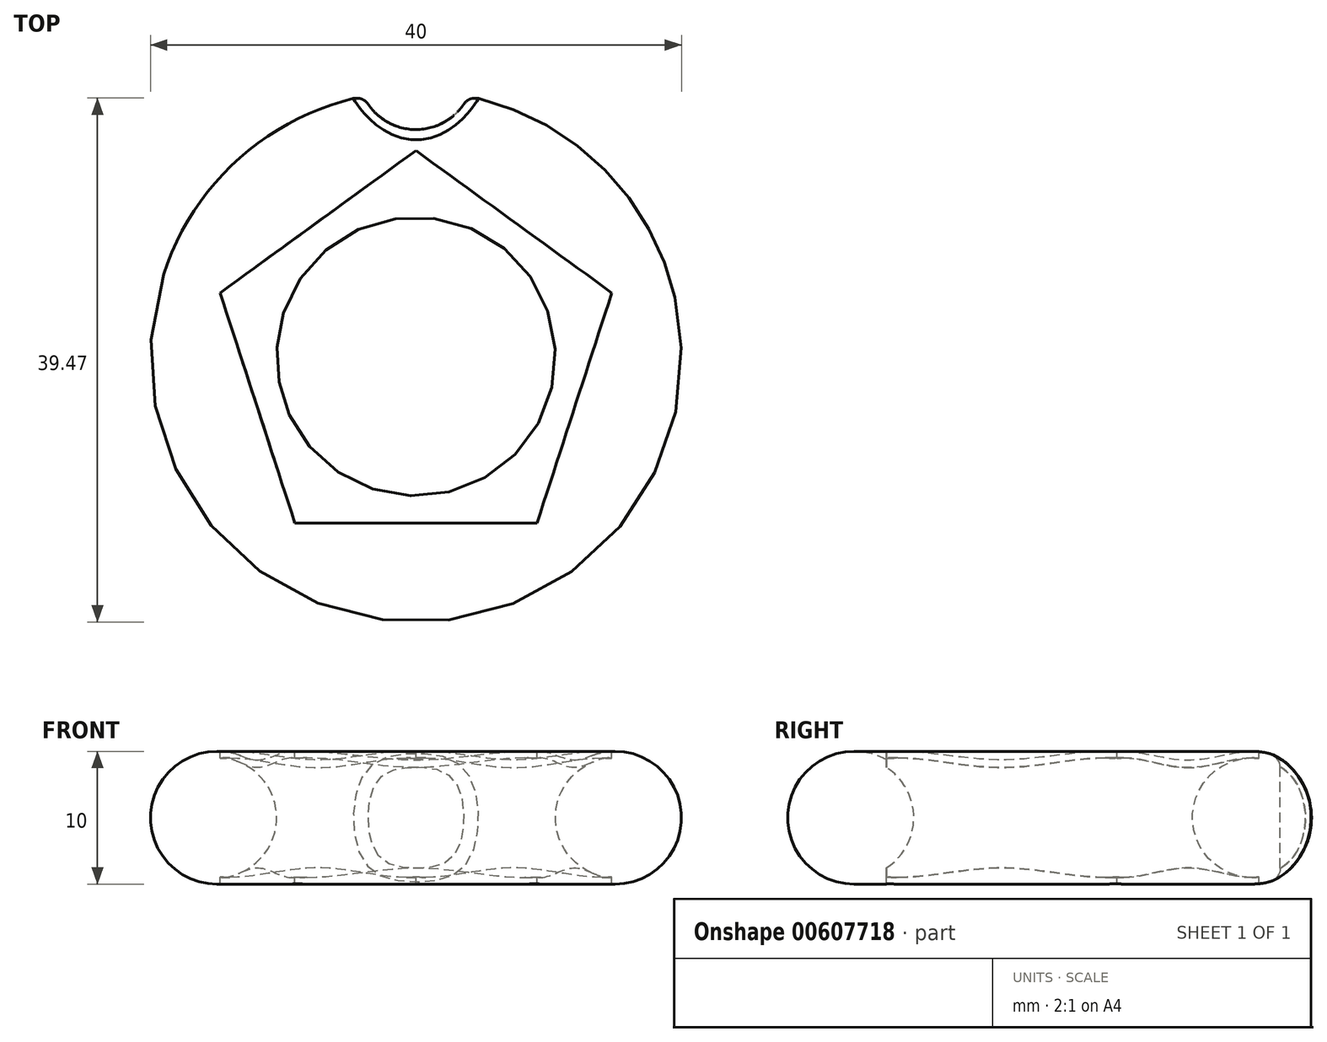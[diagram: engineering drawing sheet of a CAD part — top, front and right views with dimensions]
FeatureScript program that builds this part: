
annotation { "Feature Type Name" : "Feature", "Feature Type Description" : "" }
export const myFeature = defineFeature(function(context is Context, id is Id, definition is map)
    precondition{}
    {
        {
            var Q0;
            Q0=qCreatedBy(makeId("Front.planeOp"),FACE);
            var sketch = newSketch(context, id + "F0", { "sketchPlane" : qUnion([Q0])});
            skArc(sketch, "E0", {"start": v(-12, 9) * mm, "mid": v(-6.32, 6.03) * mm, "end": v(0, 5) * mm});
            skArc(sketch, "E1", {"start": v(-12, 9) * mm, "mid": v(-19.74, 6.58) * mm, "end": v(-15, 0) * mm});
            skLineSegment(sketch, "E2", {"start": v(-15, 0) * mm, "end": v(0, 0) * mm});
            skLineSegment(sketch, "E3", {"start": v(0, 0) * mm, "end": v(0, 5) * mm});
            skSolve(sketch);
        }
        {
            var Q0;
            Q0=makeQuery(id+"F0.imprint","IMPRINT",FACE,{"disambiguationData":[TD([[makeQuery(id+"F0.imprint","IMPRINT",EDGE,{"derivedFrom":sQuery(id+"F0.wireOp",EDGE,"E0")}),-1.0]])]});
            var Q1;
            Q1=sQuery(id+"F0.wireOp",EDGE,"E3");
            revolve(context, id + "F1", {"entities" : qUnion([Q0]), "axis" : qUnion([Q1]), "revolveType" : RevolveType.FULL});
        }
        {
            var Q0;
            Q0=qCreatedBy(makeId("Top.planeOp"),FACE);
            var sketch = newSketch(context, id + "F2", { "sketchPlane" : qUnion([Q0])});
            skCircle(sketch, "E4.cCircle", {"center": v(0, 0) * mm, "radius": 12.55 * mm, "construction": true});
            skLineSegment(sketch, "E4.0", {"start": v(0, 15.51) * mm, "end": v(14.76, 4.8) * mm});
            skLineSegment(sketch, "E4.1", {"start": v(14.76, 4.8) * mm, "end": v(9.12, -12.55) * mm});
            skLineSegment(sketch, "E4.2", {"start": v(9.12, -12.55) * mm, "end": v(-9.12, -12.55) * mm});
            skLineSegment(sketch, "E4.3", {"start": v(-9.12, -12.55) * mm, "end": v(-14.76, 4.8) * mm});
            skLineSegment(sketch, "E4.4", {"start": v(-14.76, 4.8) * mm, "end": v(0, 15.51) * mm});
            skSolve(sketch);
        }
        {
            var Q0;
            Q0 = qSketchRegion(id + "F2", true);
            extrude(context, id + "F3", {"entities" : qUnion([Q0]), "operationType" : NewBodyOperationType.REMOVE, "endBound" : BoundingType.SYMMETRIC, "oppositeDirection" : true, "depth" : 25 * mm, "offsetDistance" : 25 * mm});
        }
        {
            var Q0;
            Q0=qCreatedBy(makeId("Front.planeOp"),FACE);
            var sketch = newSketch(context, id + "F4", { "sketchPlane" : qUnion([Q0])});
            skCircle(sketch, "E5", {"center": v(-15, 5) * mm, "radius": 4.5 * mm});
            skSolve(sketch);
        }
        {
            var Q0;
            Q0 = qSketchRegion(id + "F4", true);
            var Q1;
            Q1=sQuery(id+"F0.wireOp",EDGE,"E3");
            revolve(context, id + "F5", {"operationType" : NewBodyOperationType.ADD, "entities" : qUnion([Q0]), "axis" : qUnion([Q1]), "revolveType" : RevolveType.FULL});
        }
        {
            var Q0;
            Q0=qCreatedBy(makeId("Top.planeOp"),FACE);
            var sketch = newSketch(context, id + "F6", { "sketchPlane" : qUnion([Q0])});
            skCircle(sketch, "E6", {"center": v(0, 21.44) * mm, "radius": 4.34 * mm});
            skSolve(sketch);
        }
        {
            var Q0;
            Q0=makeQuery(id+"F6.imprint","IMPRINT",FACE,{"disambiguationData":[TD([[makeQuery(id+"F6.imprint","IMPRINT",EDGE,{"derivedFrom":sQuery(id+"F6.wireOp",EDGE,"E6")}),1.0]])]});
            extrude(context, id + "F7", {"entities" : qUnion([Q0]), "operationType" : NewBodyOperationType.REMOVE, "endBound" : BoundingType.SYMMETRIC, "oppositeDirection" : true, "depth" : 25 * mm, "offsetDistance" : 25 * mm});
        }
        {
            var Q0;
            Q0=makeQuery(id+"F7.boolean.opBoolean","INTERSECT",EDGE,{"derivedFrom":[makeQuery(id+"F1.opRevolve","SWEPT_FACE",FACE,{"disambiguationData":[OSD([sQuery(id+"F0.wireOp",EDGE,"E1")])]}),makeQuery(id+"F7.opExtrude","SWEPT_FACE",FACE,{"disambiguationData":[OSD([sQuery(id+"F6.wireOp",EDGE,"E6")])]})]});
            fillet(context, id + "F8", {"entities" : qUnion([Q0]), "radius" : 1.05 * mm, "tangentPropagation" : true, "allowEdgeOverflow" : false});
        }
    });
